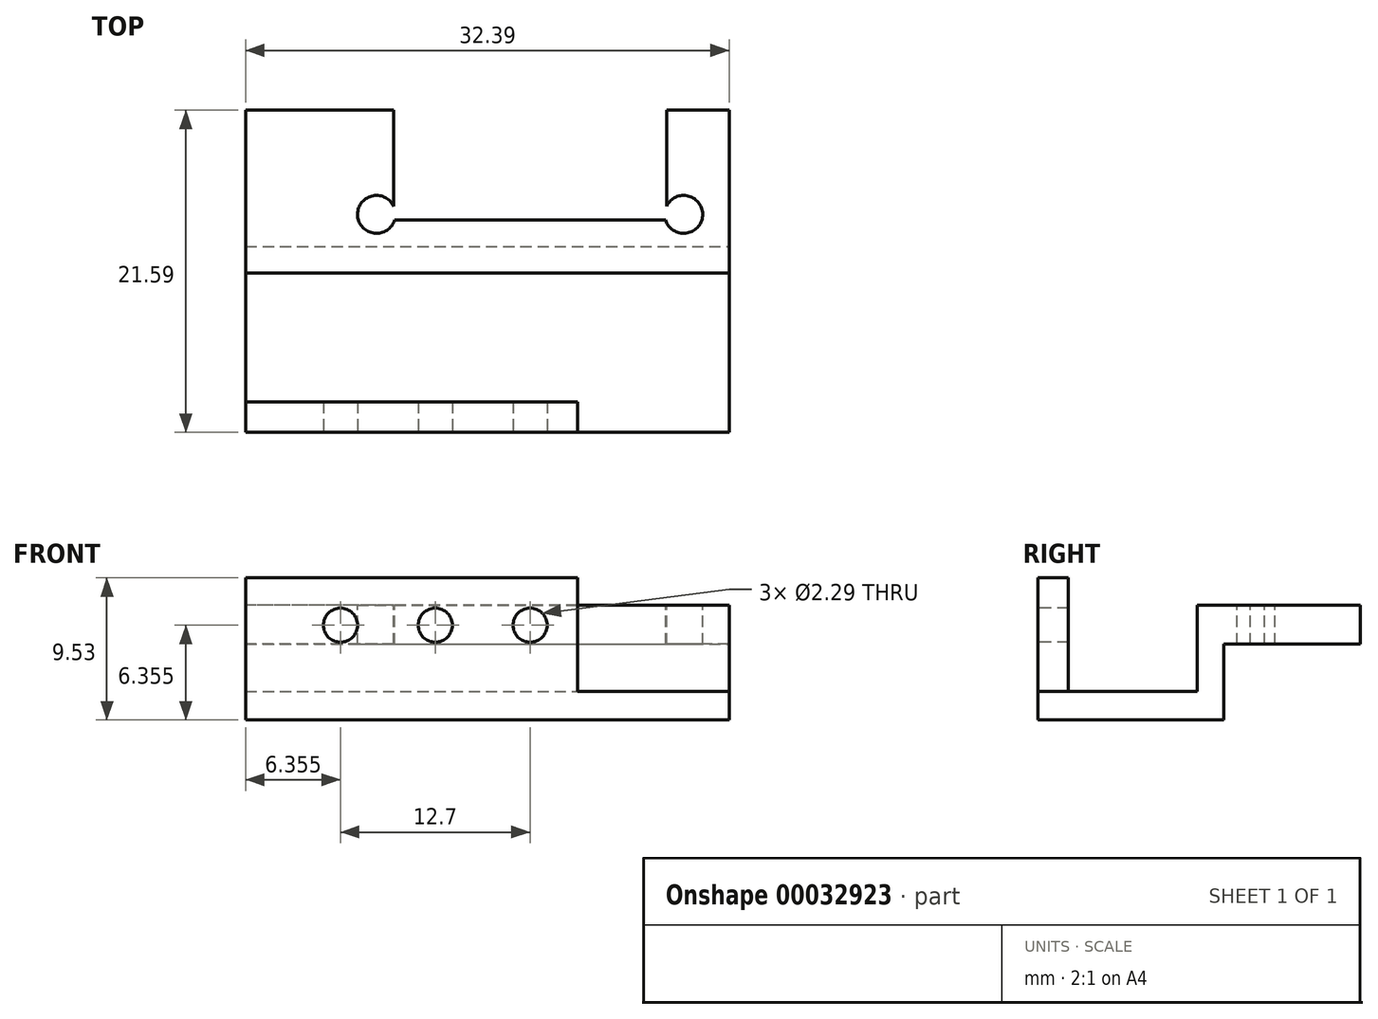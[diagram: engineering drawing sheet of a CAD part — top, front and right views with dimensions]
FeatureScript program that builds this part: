
annotation { "Feature Type Name" : "Feature", "Feature Type Description" : "" }
export const myFeature = defineFeature(function(context is Context, id is Id, definition is map)
    precondition{}
    {
        {
            var Q0;
            Q0=qCreatedBy(makeId("Front.planeOp"),FACE);
            var sketch = newSketch(context, id + "F0", { "sketchPlane" : qUnion([Q0])});
            skLineSegment(sketch, "E0.bottom", {"start": v(0, 0) * mm, "end": v(-22.23, 0) * mm});
            skLineSegment(sketch, "E0.top", {"start": v(0, 8.9) * mm, "end": v(-22.23, 8.89) * mm});
            skLineSegment(sketch, "E0.left", {"start": v(0, 0) * mm, "end": v(0, 8.9) * mm});
            skLineSegment(sketch, "E0.right", {"start": v(-22.23, 0) * mm, "end": v(-22.23, 8.89) * mm});
            skCircle(sketch, "E1", {"center": v(-3.18, 5.72) * mm, "radius": 1.14 * mm});
            skCircle(sketch, "E2", {"center": v(-9.53, 5.71) * mm, "radius": 1.14 * mm});
            skCircle(sketch, "E3", {"center": v(-15.88, 5.71) * mm, "radius": 1.14 * mm});
            skLineSegment(sketch, "E4.bottom", {"start": v(-22.23, 0) * mm, "end": v(15.88, 0) * mm, "construction": true});
            skLineSegment(sketch, "E4.top", {"start": v(-22.23, 38.1) * mm, "end": v(15.87, 38.1) * mm, "construction": true});
            skLineSegment(sketch, "E4.left", {"start": v(-22.23, 0) * mm, "end": v(-22.23, 38.1) * mm, "construction": true});
            skLineSegment(sketch, "E4.right", {"start": v(15.88, 0) * mm, "end": v(15.87, 38.1) * mm, "construction": true});
            skLineSegment(sketch, "E5", {"start": v(-22.23, 19.05) * mm, "end": v(15.87, 19.05) * mm, "construction": true});
            skLineSegment(sketch, "E6", {"start": v(-3.18, 38.1) * mm, "end": v(-3.18, 19.05) * mm, "construction": true});
            skCircle(sketch, "E7", {"center": v(-3.18, 19.05) * mm, "radius": 7.05 * mm, "construction": true});
            skPoint(sketch, "E8.trimOffspring.end.orphan", {"position": v(-3.18, 0) * mm});
            skCircle(sketch, "E9", {"center": v(-3.18, 19.05) * mm, "radius": 6 * mm, "construction": true});
            skLineSegment(sketch, "E10.rect.bottom", {"start": v(11.37, 33.65) * mm, "end": v(-17.72, 33.66) * mm, "construction": true});
            skLineSegment(sketch, "E10.rect.top", {"start": v(11.37, 4.45) * mm, "end": v(-17.72, 4.45) * mm, "construction": true});
            skLineSegment(sketch, "E10.rect.left", {"start": v(11.37, 33.65) * mm, "end": v(11.37, 4.44) * mm, "construction": true});
            skLineSegment(sketch, "E10.rect.right", {"start": v(-17.72, 33.65) * mm, "end": v(-17.72, 4.45) * mm, "construction": true});
            skSolve(sketch);
        }
        {
            var Q0;
            Q0=makeQuery(id+"F0.imprint","IMPRINT",FACE,{"disambiguationData":[TD([[makeQuery(id+"F0.imprint","IMPRINT",EDGE,{"derivedFrom":sQuery(id+"F0.wireOp",EDGE,"E0.bottom")}),-1.0]])]});
            extrude(context, id + "F1", {"entities" : qUnion([Q0]), "oppositeDirection" : true, "depth" : 2.03 * mm});
        }
        {
            var Q0;
            Q0=qCreatedBy(makeId("Right.planeOp"),FACE);
            var sketch = newSketch(context, id + "F2", { "sketchPlane" : qUnion([Q0])});
            skLineSegment(sketch, "E11.bottom", {"start": v(0, -0.64) * mm, "end": v(17.78, -0.64) * mm});
            skLineSegment(sketch, "E11.top", {"start": v(0, 1.27) * mm, "end": v(17.78, 1.27) * mm});
            skLineSegment(sketch, "E11.left", {"start": v(0, -0.64) * mm, "end": v(0, 1.27) * mm});
            skLineSegment(sketch, "E11.right", {"start": v(17.78, -0.64) * mm, "end": v(17.78, 1.27) * mm});
            skSolve(sketch);
        }
        {
            var Q0;
            Q0=makeQuery(id+"F2.imprint","IMPRINT",FACE,{"disambiguationData":[TD([[makeQuery(id+"F2.imprint","IMPRINT",EDGE,{"derivedFrom":sQuery(id+"F2.wireOp",EDGE,"E11.bottom")}),1.0]])]});
            var Q1;
            Q1=makeQuery(id+"F1.opExtrude","SWEPT_FACE",FACE,{"disambiguationData":[OSD([sQuery(id+"F0.wireOp",EDGE,"E0.right")])]});
            extrude(context, id + "F3", {"entities" : qUnion([Q0]), "operationType" : NewBodyOperationType.ADD, "endBound" : BoundingType.UP_TO_SURFACE, "oppositeDirection" : true, "endBoundEntityFace" : qUnion([Q1]), "depth" : 25.4 * mm});
        }
        {
            var Q0;
            Q0=qSketchRegion(id+"F2",true);
            extrude(context, id + "F4", {"entities" : qUnion([Q0]), "operationType" : NewBodyOperationType.ADD, "depth" : 10.16 * mm});
        }
        {
            var Q0;
            Q0=makeQuery(id+"F3.boolean.opBoolean","MERGE",FACE,{"derivedFrom":[makeQuery(id+"F1.opExtrude","SWEPT_FACE",FACE,{"disambiguationData":[OSD([sQuery(id+"F0.wireOp",EDGE,"E0.right")])]}),makeQuery(id+"F3.opExtrude","CAP_FACE",FACE,{"disambiguationData":[OSD([sQuery(id+"F2.wireOp",EDGE,"E11.bottom"),sQuery(id+"F2.wireOp",EDGE,"E11.top"),sQuery(id+"F2.wireOp",EDGE,"E11.left"),sQuery(id+"F2.wireOp",EDGE,"E11.right")])],"isStart":false})]});
            var sketch = newSketch(context, id + "F5", { "sketchPlane" : qUnion([Q0])});
            skLineSegment(sketch, "E12.bottom", {"start": v(-21.6, -0.63) * mm, "end": v(-10.67, -0.63) * mm});
            skLineSegment(sketch, "E12.top", {"start": v(-21.6, 7.05) * mm, "end": v(-10.67, 7.05) * mm});
            skLineSegment(sketch, "E12.left", {"start": v(-21.6, -0.63) * mm, "end": v(-21.6, 7.05) * mm});
            skLineSegment(sketch, "E12.right", {"start": v(-10.67, -0.63) * mm, "end": v(-10.67, 7.05) * mm});
            skSolve(sketch);
        }
        {
            var Q0;
            {var subQ0=sQuery(id+"F2.wireOp",EDGE,"E11.top");Q0=makeQuery(id+"F4.boolean.opBoolean","MERGE",FACE,{"derivedFrom":[makeQuery(id+"F3.opExtrude","SWEPT_FACE",FACE,{"disambiguationData":[OSD([subQ0])]}),makeQuery(id+"F4.opExtrude","SWEPT_FACE",FACE,{"disambiguationData":[OSD([subQ0])]})]});}
            var sketch = newSketch(context, id + "F6", { "sketchPlane" : qUnion([Q0])});
            skLineSegment(sketch, "E13.bottom", {"start": v(5.97, 17.78) * mm, "end": v(-12.32, 17.78) * mm});
            skLineSegment(sketch, "E13.top", {"start": v(5.97, 14.22) * mm, "end": v(-12.32, 14.22) * mm});
            skLineSegment(sketch, "E13.left", {"start": v(5.97, 24.38) * mm, "end": v(5.97, 14.22) * mm});
            skLineSegment(sketch, "E13.right", {"start": v(-12.32, 24.38) * mm, "end": v(-12.32, 14.22) * mm});
            skLineSegment(sketch, "E14", {"start": v(-3.18, 19.13) * mm, "end": v(-3.18, 0) * mm, "construction": true});
            skLineSegment(sketch, "E15", {"start": v(-12.32, 24.38) * mm, "end": v(5.97, 24.38) * mm});
            skSolve(sketch);
        }
        {
            var Q0;
            Q0=qSketchRegion(id+"F5",true);
            var Q1;
            Q1=makeQuery(id+"F4.opExtrude","CAP_FACE",FACE,{"disambiguationData":[OSD([sQuery(id+"F2.wireOp",EDGE,"E11.bottom"),sQuery(id+"F2.wireOp",EDGE,"E11.top"),sQuery(id+"F2.wireOp",EDGE,"E11.left"),sQuery(id+"F2.wireOp",EDGE,"E11.right")])],"isStart":false});
            extrude(context, id + "F7", {"entities" : qUnion([Q0]), "operationType" : NewBodyOperationType.ADD, "endBound" : BoundingType.UP_TO_SURFACE, "oppositeDirection" : true, "endBoundEntityFace" : qUnion([Q1]), "depth" : 25.4 * mm});
        }
        {
            var Q0;
            Q0=qSketchRegion(id+"F6",true);
            var Q1;
            {var subQ0=sQuery(id+"F2.wireOp",EDGE,"E11.bottom");Q1=makeQuery(id+"F4.boolean.opBoolean","MERGE",FACE,{"derivedFrom":[makeQuery(id+"F3.boolean.opBoolean","MERGE",FACE,{"derivedFrom":[makeQuery(id+"F1.opExtrude","SWEPT_FACE",FACE,{"disambiguationData":[OSD([sQuery(id+"F0.wireOp",EDGE,"E0.bottom")])]}),makeQuery(id+"F3.opExtrude","SWEPT_FACE",FACE,{"disambiguationData":[OSD([subQ0])]})]}),makeQuery(id+"F4.opExtrude","SWEPT_FACE",FACE,{"disambiguationData":[OSD([subQ0])]})]});}
            extrude(context, id + "F8", {"entities" : qUnion([Q0]), "operationType" : NewBodyOperationType.REMOVE, "endBound" : BoundingType.SYMMETRIC, "oppositeDirection" : true, "endBoundEntityFace" : qUnion([Q1]), "depth" : 25.4 * mm});
        }
        {
            var Q0;
            Q0=makeQuery(id+"F7.opExtrude","SWEPT_FACE",FACE,{"disambiguationData":[OSD([sQuery(id+"F5.wireOp",EDGE,"E12.top")])]});
            var sketch = newSketch(context, id + "F9", { "sketchPlane" : qUnion([Q0])});
            skCircle(sketch, "E16", {"center": v(-13.46, 14.6) * mm, "radius": 1.27 * mm});
            skCircle(sketch, "E17", {"center": v(7.11, 14.6) * mm, "radius": 1.27 * mm});
            skSolve(sketch);
        }
        {
            var Q0;
            Q0=qSketchRegion(id+"F9",true);
            extrude(context, id + "F10", {"entities" : qUnion([Q0]), "operationType" : NewBodyOperationType.REMOVE, "oppositeDirection" : true, "depth" : 25.4 * mm});
        }
        {
            var Q0;
            {var subQ0=sQuery(id+"F2.wireOp",EDGE,"E11.bottom");Q0=makeQuery(id+"F4.boolean.opBoolean","MERGE",FACE,{"derivedFrom":[makeQuery(id+"F3.boolean.opBoolean","MERGE",FACE,{"derivedFrom":[makeQuery(id+"F1.opExtrude","SWEPT_FACE",FACE,{"disambiguationData":[OSD([sQuery(id+"F0.wireOp",EDGE,"E0.bottom")])]}),makeQuery(id+"F3.opExtrude","SWEPT_FACE",FACE,{"disambiguationData":[OSD([subQ0])]})]}),makeQuery(id+"F4.opExtrude","SWEPT_FACE",FACE,{"disambiguationData":[OSD([subQ0])]})]});}
            var sketch = newSketch(context, id + "F11", { "sketchPlane" : qUnion([Q0])});
            skLineSegment(sketch, "E18.bottom", {"start": v(-22.23, -22.1) * mm, "end": v(10.16, -22.1) * mm});
            skLineSegment(sketch, "E18.top", {"start": v(-22.23, -12.45) * mm, "end": v(10.16, -12.45) * mm});
            skLineSegment(sketch, "E18.left", {"start": v(-22.23, -22.1) * mm, "end": v(-22.23, -12.45) * mm});
            skLineSegment(sketch, "E18.right", {"start": v(10.16, -22.1) * mm, "end": v(10.16, -12.45) * mm});
            skSolve(sketch);
        }
        {
            var Q0;
            Q0=makeQuery(id+"F11.imprint","IMPRINT",FACE,{"disambiguationData":[TD([[makeQuery(id+"F11.imprint","IMPRINT",EDGE,{"derivedFrom":sQuery(id+"F11.wireOp",EDGE,"E18.top")}),-1.0]])]});
            extrude(context, id + "F12", {"entities" : qUnion([Q0]), "operationType" : NewBodyOperationType.REMOVE, "oppositeDirection" : true, "depth" : 5.08 * mm});
        }
    });
